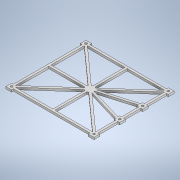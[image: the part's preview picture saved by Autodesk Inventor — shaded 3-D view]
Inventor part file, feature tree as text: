
AUTODESK INVENTOR PART (.ipt)
format: ipt  version: 2020 (Build 240168000, 168)  size: 288,768 bytes
history: native  units: in
note: dims shown in document units (in); Inventor stores cm internally (conversion verified against a paired STEP export)
features: extrude x1, sketch x1
ambient origin geometry x8: Origin, YZ Plane, XZ Plane, XY Plane, X Axis, Y Axis, Z Axis, Center Point
bodies: Solid1 (feature_tree)
feature tree (2):
  extrude  "Extrusion1"  Depth=0.1181in
  sketch  "Sketch1"  dims[d0=5.9055in d1=4.7244in d2=0.5114in d3=0.0157in d4=0.1575in d5=0.315in d6=0.315in d7=0.315in d8=0.315in d9=0.4724in d10=0.122in d11=0.122in d13=0.4724in d14=0.1181in d15=0.1181in d16=0.1181in d17=0.1181in d18=0.1181in d19=0.1181in d20=0.1181in d21=0.1181in d22=0.1181in d23=0.1181in d24=0.1181in d25=0.1181in d26=0.1181in d27=0.0in]
